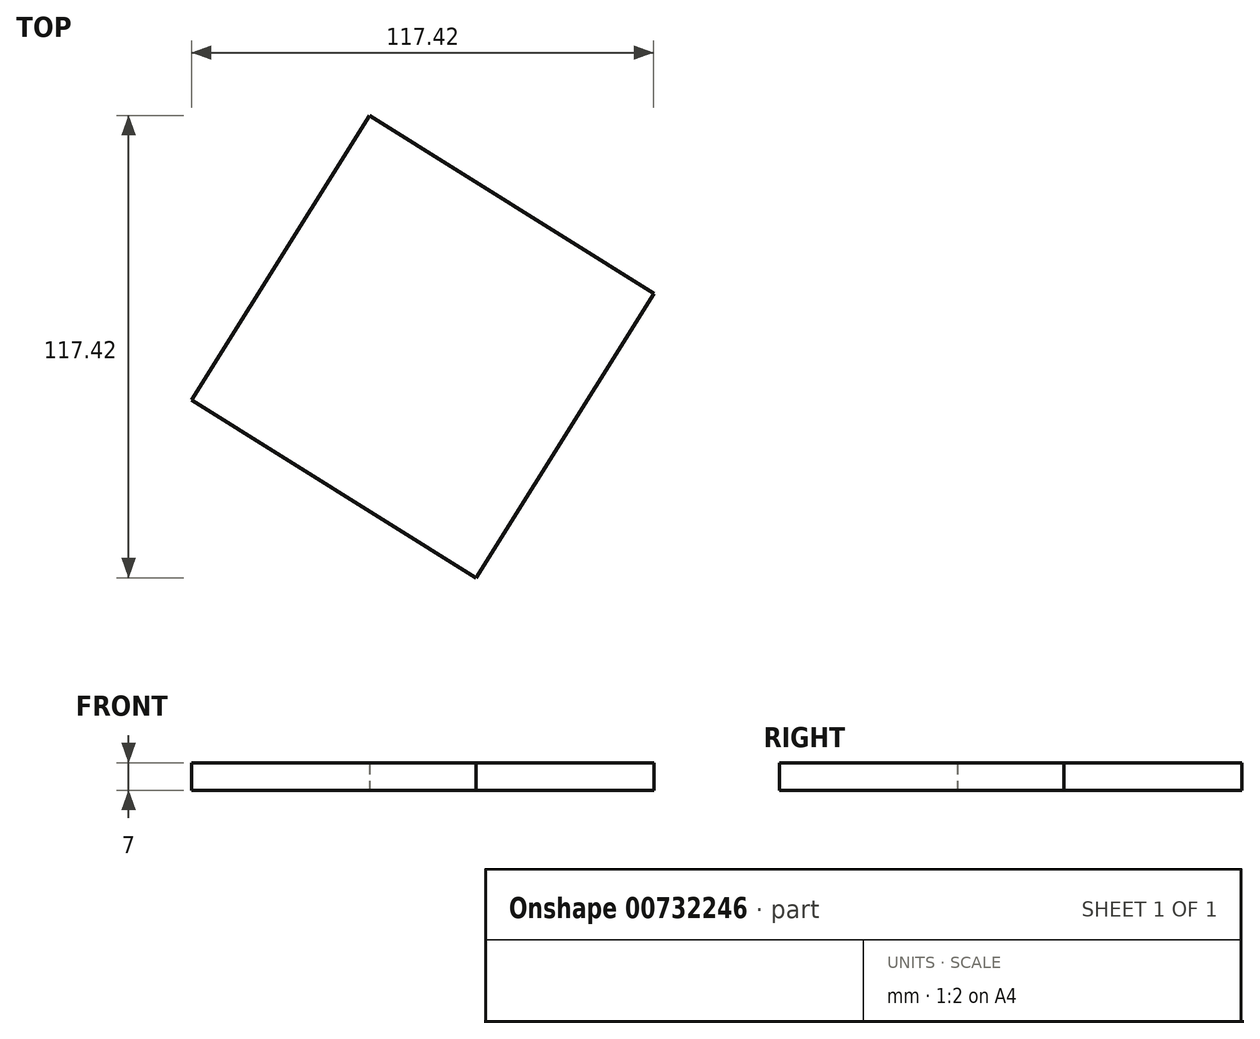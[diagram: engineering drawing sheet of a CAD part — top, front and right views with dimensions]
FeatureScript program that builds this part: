
annotation { "Feature Type Name" : "Feature", "Feature Type Description" : "" }
export const myFeature = defineFeature(function(context is Context, id is Id, definition is map)
    precondition{}
    {
        {
            var Q0;
            Q0=qCreatedBy(makeId("Top.planeOp"),FACE);
            var sketch = newSketch(context, id + "F0", { "sketchPlane" : qUnion([Q0])});
            skCircle(sketch, "E0.cCircle", {"center": v(0, 0) * mm, "radius": 42.6 * mm, "construction": true});
            skLineSegment(sketch, "E0.0", {"start": v(58.71, 13.53) * mm, "end": v(13.53, -58.71) * mm});
            skLineSegment(sketch, "E0.1", {"start": v(13.53, -58.71) * mm, "end": v(-58.71, -13.53) * mm});
            skLineSegment(sketch, "E0.2", {"start": v(-58.71, -13.53) * mm, "end": v(-13.53, 58.71) * mm});
            skLineSegment(sketch, "E0.3", {"start": v(-13.53, 58.71) * mm, "end": v(58.71, 13.53) * mm});
            skPoint(sketch, "E0.0.midPoint", {"position": v(36.12, -22.6) * mm});
            skSolve(sketch);
        }
        {
            var Q0;
            Q0=makeQuery(id+"F0.imprint","IMPRINT",FACE,{"disambiguationData":[TD([[makeQuery(id+"F0.imprint","IMPRINT",EDGE,{"derivedFrom":sQuery(id+"F0.wireOp",EDGE,"E0.0")}),-1.0]])]});
            extrude(context, id + "F1", {"entities" : qUnion([Q0]), "depth" : 7 * mm, "offsetDistance" : 25 * mm});
        }
    });
